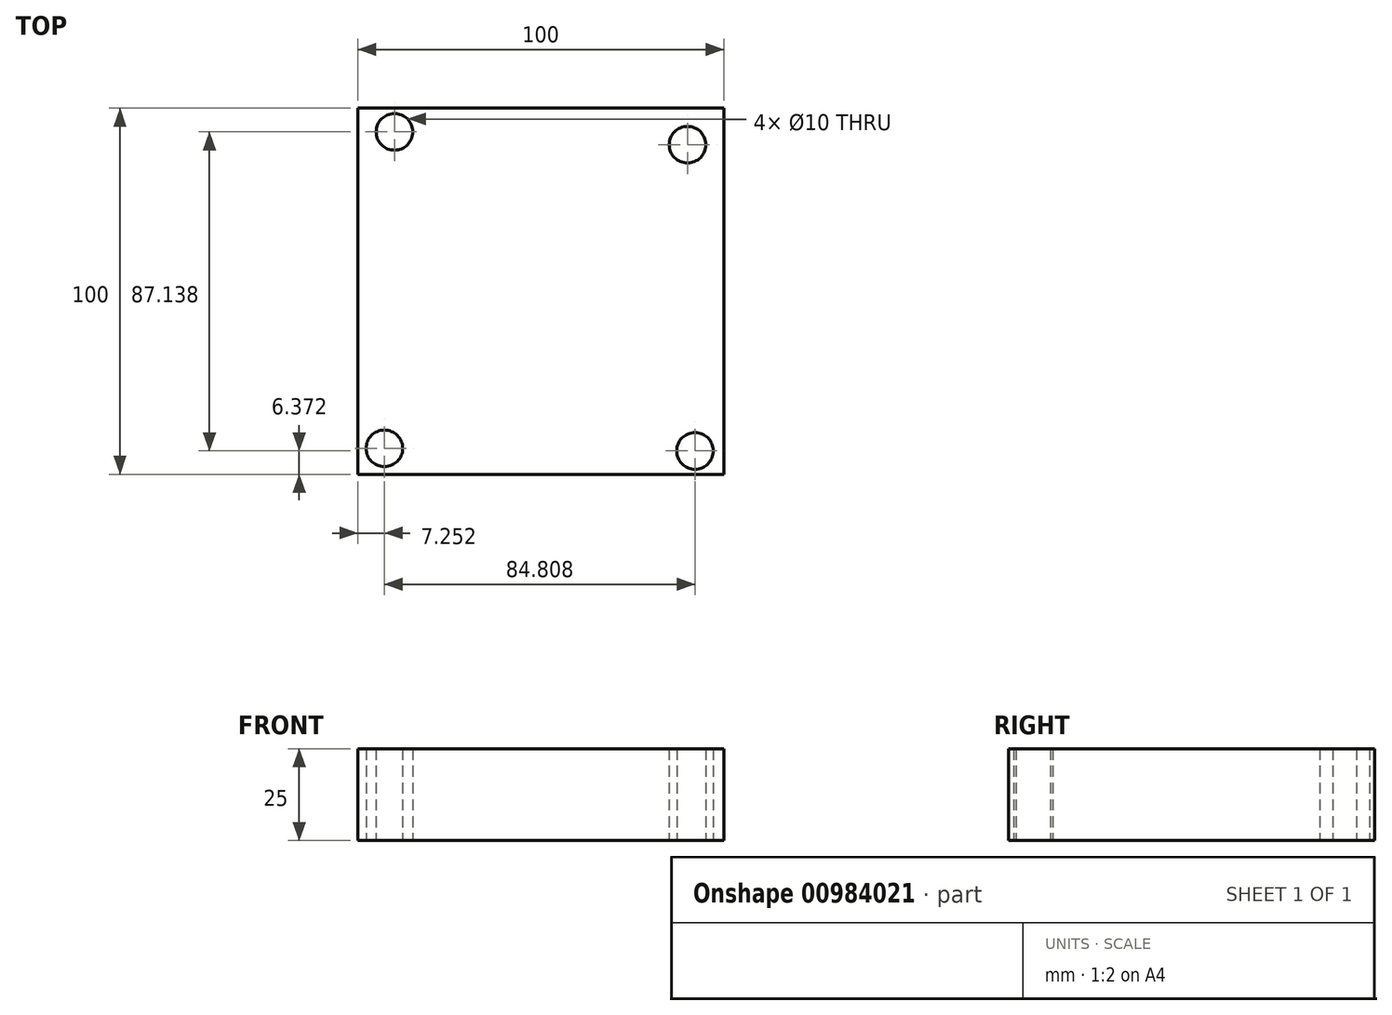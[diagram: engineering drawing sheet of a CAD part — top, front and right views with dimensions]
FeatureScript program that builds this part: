
annotation { "Feature Type Name" : "Feature", "Feature Type Description" : "" }
export const myFeature = defineFeature(function(context is Context, id is Id, definition is map)
    precondition{}
    {
        {
            var Q0;
            Q0=qCreatedBy(makeId("Top.planeOp"),FACE);
            var sketch = newSketch(context, id + "F0", { "sketchPlane" : qUnion([Q0])});
            skLineSegment(sketch, "E0.bottom", {"start": v(-28.57, 52.04) * mm, "end": v(71.43, 52.04) * mm});
            skLineSegment(sketch, "E0.top", {"start": v(-28.57, -47.96) * mm, "end": v(71.43, -47.96) * mm});
            skLineSegment(sketch, "E0.left", {"start": v(-28.57, 52.04) * mm, "end": v(-28.57, -47.96) * mm});
            skLineSegment(sketch, "E0.right", {"start": v(71.43, 52.04) * mm, "end": v(71.43, -47.96) * mm});
            skCircle(sketch, "E1", {"center": v(-18.57, 45.55) * mm, "radius": 5 * mm});
            skCircle(sketch, "E2", {"center": v(61.43, 42.04) * mm, "radius": 5 * mm});
            skCircle(sketch, "E3", {"center": v(63.49, -41.59) * mm, "radius": 5 * mm});
            skCircle(sketch, "E4", {"center": v(-21.32, -40.89) * mm, "radius": 5 * mm});
            skSolve(sketch);
        }
        {
            var Q0;
            Q0 = qSketchRegion(id + "F0", true);
            extrude(context, id + "F1", {"entities" : qUnion([Q0]), "depth" : 25 * mm, "offsetDistance" : 25 * mm});
        }
    });
